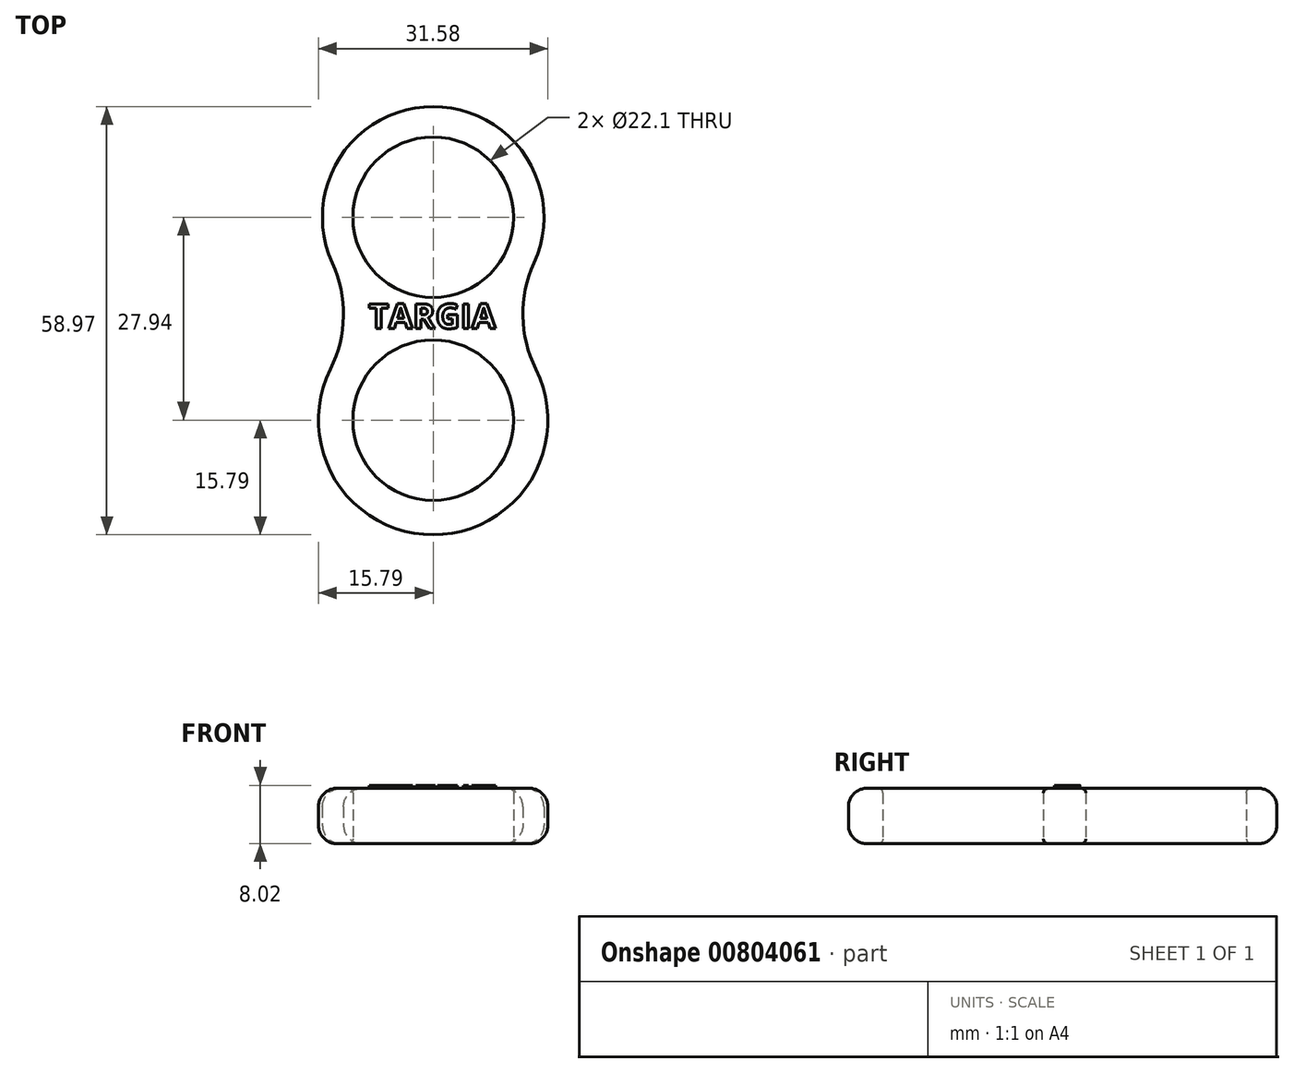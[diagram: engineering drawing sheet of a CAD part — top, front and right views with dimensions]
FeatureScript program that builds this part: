
annotation { "Feature Type Name" : "Feature", "Feature Type Description" : "" }
export const myFeature = defineFeature(function(context is Context, id is Id, definition is map)
    precondition{}
    {
        {
            var Q0;
            Q0=qCreatedBy(makeId("Top.planeOp"),FACE);
            var sketch = newSketch(context, id + "F0", { "sketchPlane" : qUnion([Q0])});
            skCircle(sketch, "E0", {"center": v(0, 0) * mm, "radius": 11.05 * mm});
            skCircle(sketch, "E1", {"center": v(0, 27.94) * mm, "radius": 11.05 * mm});
            skArc(sketch, "E2", {"start": v(13.87, 21.62) * mm, "mid": v(0, 43.18) * mm, "end": v(-13.87, 21.62) * mm});
            skArc(sketch, "E3", {"start": v(13.87, 21.62) * mm, "mid": v(12.35, 14.3) * mm, "end": v(14.13, 7.05) * mm});
            skArc(sketch, "E4.MirrorCS", {"start": v(-13.87, 21.62) * mm, "mid": v(-12.35, 14.3) * mm, "end": v(-14.13, 7.05) * mm});
            skArc(sketch, "E5.trimOffspring", {"start": v(-14.13, 7.05) * mm, "mid": v(0, -15.79) * mm, "end": v(14.13, 7.05) * mm});
            skSolve(sketch);
        }
        {
            var Q0;
            Q0=makeQuery(id+"F0.imprint","IMPRINT",FACE,{"disambiguationData":[TD([[makeQuery(id+"F0.imprint","IMPRINT",EDGE,{"derivedFrom":sQuery(id+"F0.wireOp",EDGE,"E0")}),-1.0]])]});
            extrude(context, id + "F1", {"entities" : qUnion([Q0]), "depth" : 7.62 * mm, "offsetDistance" : 25.4 * mm});
        }
        {
            var Q0;
            Q0=makeQuery(id+"F1.opExtrude","CAP_EDGE",EDGE,{"disambiguationData":[OSD([sQuery(id+"F0.wireOp",EDGE,"E3")])],"isStart":false});
            var Q1;
            Q1=makeQuery(id+"F1.opExtrude","CAP_EDGE",EDGE,{"disambiguationData":[OSD([sQuery(id+"F0.wireOp",EDGE,"E3")])],"isStart":true});
            fillet(context, id + "F2", {"entities" : qUnion([Q0, Q1]), "radius" : 2.54 * mm, "tangentPropagation" : true, "allowEdgeOverflow" : false});
        }
        {
            var Q0;
            Q0=makeQuery(id+"F1.opExtrude","CAP_EDGE",EDGE,{"disambiguationData":[OSD([sQuery(id+"F0.wireOp",EDGE,"E0")])],"isStart":false});
            var Q1;
            Q1=makeQuery(id+"F1.opExtrude","CAP_EDGE",EDGE,{"disambiguationData":[OSD([sQuery(id+"F0.wireOp",EDGE,"E1")])],"isStart":false});
            var Q2;
            Q2=makeQuery(id+"F1.opExtrude","CAP_EDGE",EDGE,{"disambiguationData":[OSD([sQuery(id+"F0.wireOp",EDGE,"E0")])],"isStart":true});
            var Q3;
            Q3=makeQuery(id+"F1.opExtrude","CAP_EDGE",EDGE,{"disambiguationData":[OSD([sQuery(id+"F0.wireOp",EDGE,"E1")])],"isStart":true});
            fillet(context, id + "F3", {"entities" : qUnion([Q0, Q1, Q2, Q3]), "radius" : 0.64 * mm, "tangentPropagation" : true, "allowEdgeOverflow" : false});
        }
        {
            var Q0;
            Q0=makeQuery(id+"F1.opExtrude","CAP_FACE",FACE,{"disambiguationData":[OSD([sQuery(id+"F0.wireOp",EDGE,"E0"),sQuery(id+"F0.wireOp",EDGE,"E1"),sQuery(id+"F0.wireOp",EDGE,"E2"),sQuery(id+"F0.wireOp",EDGE,"E3"),sQuery(id+"F0.wireOp",EDGE,"E4.MirrorCS"),sQuery(id+"F0.wireOp",EDGE,"E5.trimOffspring")])],"isStart":false});
            var sketch = newSketch(context, id + "F4", { "sketchPlane" : qUnion([Q0])});
            skText(sketch, "E6", { "text": "TARGIA", "fontName": "OpenSans-Bold.ttf"});
            const initialGuessF4  = {"E6": [-0.00886, 0.01262, 1, 0, 0.00342]};
            skSetInitialGuess(sketch, initialGuessF4);
            skSolve(sketch);
        }
        {
            var Q0;
            Q0 = qSketchRegion(id + "F4", true);
            extrude(context, id + "F5", {"entities" : qUnion([Q0]), "operationType" : NewBodyOperationType.ADD, "depth" : 0.4 * mm, "offsetDistance" : 25.4 * mm});
        }
    });
